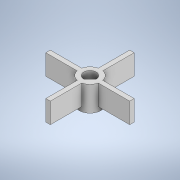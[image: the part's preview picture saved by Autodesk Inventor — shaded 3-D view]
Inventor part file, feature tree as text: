
AUTODESK INVENTOR PART (.ipt)
format: ipt  version: 2022 (Build 260153000, 153)  size: 140,800 bytes
history: native  units: mm
features: extrude x3, sketch x3
ambient origin geometry x8: Origin, YZ Plane, XZ Plane, XY Plane, X Axis, Y Axis, Z Axis, Center Point
bodies: Solid1 (feature_tree)
feature tree (6):
  extrude  "Extrusion1"  Depth=9.0mm TaperAngle=0.0deg
  extrude  "Extrusion2"  Depth=2.0mm
  extrude  "Extrusion3"  Depth=37.0mm
  sketch  "Sketch1"  dims[d0=38.0mm d1=10.0mm d2=9.0mm d3=0.0mm]
  sketch  "Sketch2"  dims[d4=2.0mm d5=0.0mm d6=5.5mm]
  sketch  "Sketch3"  dims[d7=0.0mm d8=0.0mm d9=37.0mm d10=9.5mm d11=9.5mm d12=35.0mm]
